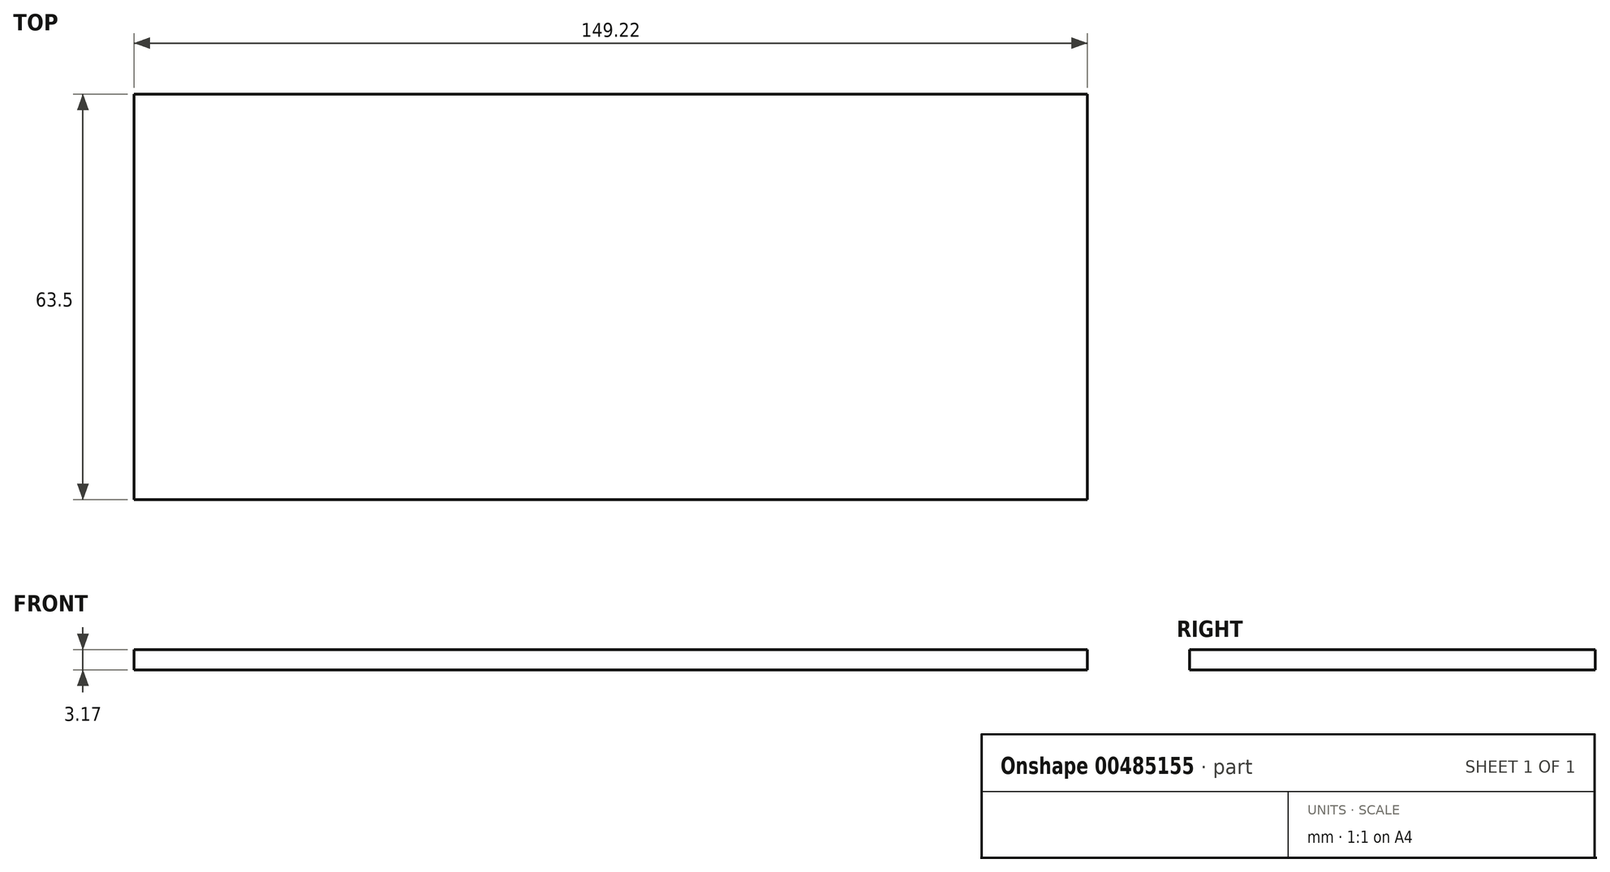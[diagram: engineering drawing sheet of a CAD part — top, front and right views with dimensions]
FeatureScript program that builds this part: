
annotation { "Feature Type Name" : "Feature", "Feature Type Description" : "" }
export const myFeature = defineFeature(function(context is Context, id is Id, definition is map)
    precondition{}
    {
        {
            var Q0;
            Q0=qCreatedBy(makeId("Top.planeOp"),FACE);
            var sketch = newSketch(context, id + "F0", { "sketchPlane" : qUnion([Q0])});
            skLineSegment(sketch, "E0.bottom", {"start": v(-74.61, -31.75) * mm, "end": v(74.61, -31.75) * mm});
            skLineSegment(sketch, "E0.top", {"start": v(-74.61, 31.75) * mm, "end": v(74.61, 31.75) * mm});
            skLineSegment(sketch, "E0.left", {"start": v(-74.61, -31.75) * mm, "end": v(-74.61, 31.75) * mm});
            skLineSegment(sketch, "E0.right", {"start": v(74.61, -31.75) * mm, "end": v(74.61, 31.75) * mm});
            skPoint(sketch, "E0.middle", {"position": v(0, 0) * mm});
            skSolve(sketch);
        }
        {
            var Q0;
            Q0=makeQuery(id+"F0.imprint","IMPRINT",FACE,{"disambiguationData":[TD([[makeQuery(id+"F0.imprint","IMPRINT",EDGE,{"derivedFrom":sQuery(id+"F0.wireOp",EDGE,"E0.bottom")}),1.0]])]});
            extrude(context, id + "F1", {"entities" : qUnion([Q0]), "depth" : 3.17 * mm});
        }
    });
